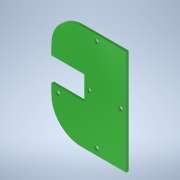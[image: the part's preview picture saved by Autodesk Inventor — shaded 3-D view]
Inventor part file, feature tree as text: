
AUTODESK INVENTOR PART (.ipt)
format: ipt  version: 2022 (Build 260153000, 153)  size: 132,608 bytes
history: native  units: mm
features: sketch x3, extrude x2, other x1, fillet x1, hole x1
ambient origin geometry x8: Origin, YZ Plane, XZ Plane, XY Plane, X Axis, Y Axis, Z Axis, Center Point
bodies: Body1 (feature_tree)
feature tree (8):
  other  "ソリッド1"
  extrude  "押し出し1"  Depth=50.0mm
  extrude  "押し出し2"  Depth=70.0mm
  fillet  "フィレット1"  Radius=1.6mm
  hole  "穴1"  [1 undecoded]
  sketch  "スケッチ1"
  sketch  "スケッチ2"
  sketch  "スケッチ3"
note: 1 required parameter value undecoded (feature->parameter linkage not recoverable at this tier; creation-order binding heuristic only, values carry confidence <= 0.55)
